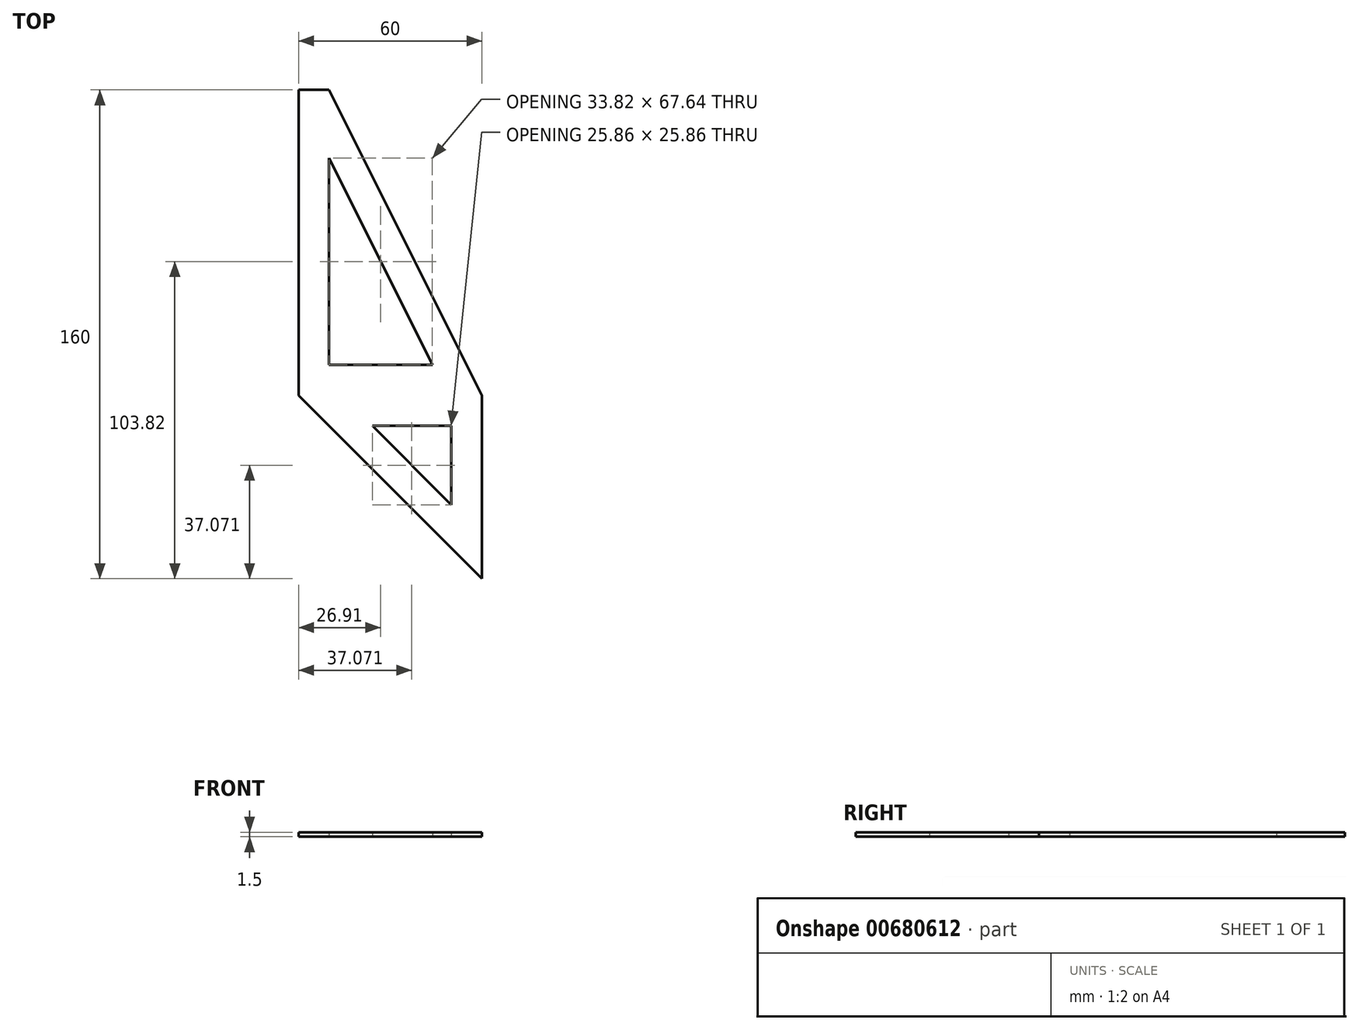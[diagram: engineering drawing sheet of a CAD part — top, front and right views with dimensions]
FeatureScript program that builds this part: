
annotation { "Feature Type Name" : "Feature", "Feature Type Description" : "" }
export const myFeature = defineFeature(function(context is Context, id is Id, definition is map)
    precondition{}
    {
        {
            var Q0;
            Q0=qCreatedBy(makeId("Top.planeOp"),FACE);
            var sketch = newSketch(context, id + "F0", { "sketchPlane" : qUnion([Q0])});
            skLineSegment(sketch, "E0", {"start": v(0, 0) * mm, "end": v(0, 100) * mm});
            skLineSegment(sketch, "E1", {"start": v(0, 100) * mm, "end": v(10, 100) * mm});
            skLineSegment(sketch, "E2", {"start": v(10, 100) * mm, "end": v(60, 0) * mm});
            skLineSegment(sketch, "E3", {"start": v(60, 0) * mm, "end": v(60, -60) * mm});
            skLineSegment(sketch, "E4", {"start": v(60, -60) * mm, "end": v(0, 0) * mm});
            skLineSegment(sketch, "E5", {"start": v(0, 0) * mm, "end": v(60, 0) * mm});
            skLineSegment(sketch, "E6.0", {"start": v(10, 10) * mm, "end": v(10, 77.64) * mm});
            skLineSegment(sketch, "E6.1", {"start": v(10, 10) * mm, "end": v(43.82, 10) * mm});
            skLineSegment(sketch, "E6.2", {"start": v(10, 77.64) * mm, "end": v(43.82, 10) * mm});
            skLineSegment(sketch, "E7.0", {"start": v(50, -35.86) * mm, "end": v(24.14, -10) * mm});
            skLineSegment(sketch, "E7.1", {"start": v(50, -10) * mm, "end": v(50, -35.86) * mm});
            skLineSegment(sketch, "E7.2", {"start": v(24.14, -10) * mm, "end": v(50, -10) * mm});
            skSolve(sketch);
        }
        {
            var Q0;
            Q0 = qSketchRegion(id + "F0", true);
            extrude(context, id + "F1", {"entities" : qUnion([Q0]), "depth" : 1.5 * mm, "offsetDistance" : 25 * mm});
        }
    });
